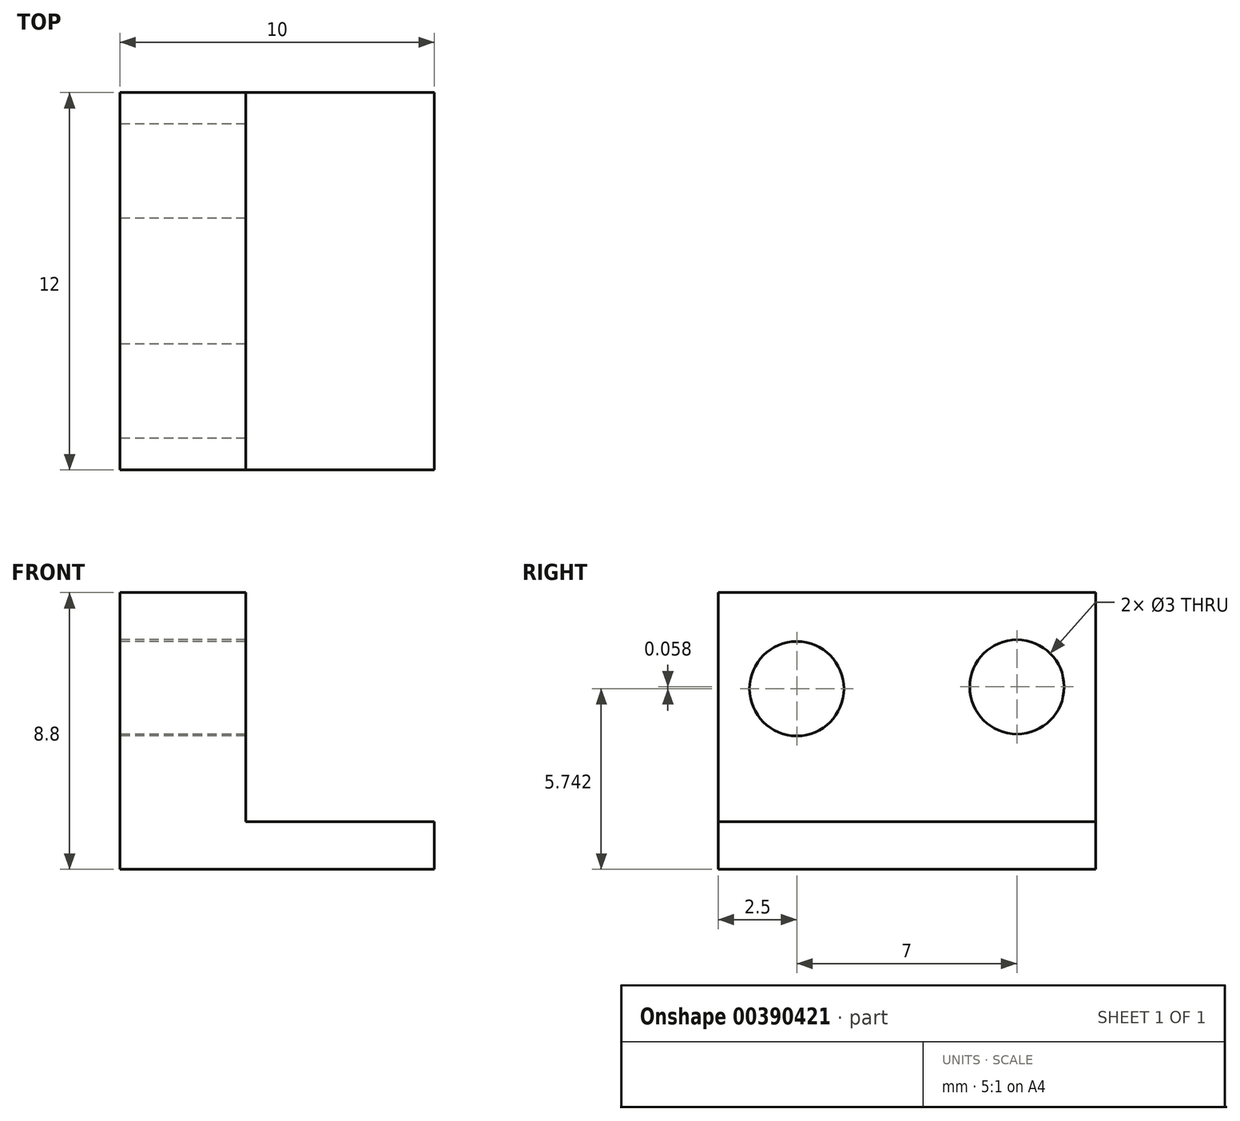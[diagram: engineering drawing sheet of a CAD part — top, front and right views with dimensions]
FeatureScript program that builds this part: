
annotation { "Feature Type Name" : "Feature", "Feature Type Description" : "" }
export const myFeature = defineFeature(function(context is Context, id is Id, definition is map)
    precondition{}
    {
        {
            var Q0;
            Q0=qCreatedBy(makeId("Front.planeOp"),FACE);
            var sketch = newSketch(context, id + "F0", { "sketchPlane" : qUnion([Q0])});
            skLineSegment(sketch, "E0.bottom", {"start": v(2, -4.4) * mm, "end": v(-2, -4.4) * mm});
            skLineSegment(sketch, "E0.top", {"start": v(2, 4.4) * mm, "end": v(-2, 4.4) * mm});
            skLineSegment(sketch, "E0.left", {"start": v(2, -4.4) * mm, "end": v(2, 4.4) * mm});
            skLineSegment(sketch, "E0.right", {"start": v(-2, -4.4) * mm, "end": v(-2, 4.4) * mm});
            skPoint(sketch, "E0.middle", {"position": v(0, 0) * mm});
            skLineSegment(sketch, "E1.bottom", {"start": v(2, -2.89) * mm, "end": v(8, -2.89) * mm});
            skLineSegment(sketch, "E1.top", {"start": v(2, -4.4) * mm, "end": v(8, -4.4) * mm});
            skLineSegment(sketch, "E1.right", {"start": v(8, -2.89) * mm, "end": v(8, -4.4) * mm});
            skSolve(sketch);
        }
        {
            var Q0;
            {var subQ0=sQuery(id+"F0.wireOp",EDGE,"E1.bottom");Q0=makeQuery(id+"F0.imprint","IMPRINT",FACE,{"disambiguationData":[TD([[makeQuery(id+"F0.imprint","IMPRINT",EDGE,{"derivedFrom":subQ0}),-1.0]])]});}
            var Q1;
            {var subQ3=sQuery(id+"F0.wireOp",EDGE,"E0.bottom");Q1=makeQuery(id+"F0.imprint","IMPRINT",FACE,{"disambiguationData":[TD([[makeQuery(id+"F0.imprint","IMPRINT",EDGE,{"derivedFrom":subQ3}),-1.0]])]});}
            extrude(context, id + "F1", {"entities" : qUnion([Q0, Q1]), "depth" : 12 * mm});
        }
        {
            var Q0;
            Q0=makeQuery(id+"F1.opExtrude","SWEPT_FACE",FACE,{"disambiguationData":[OSD([sQuery(id+"F0.wireOp",EDGE,"E0.right")])]});
            var sketch = newSketch(context, id + "F2", { "sketchPlane" : qUnion([Q0])});
            skCircle(sketch, "E2", {"center": v(2.5, 1.4) * mm, "radius": 1.5 * mm});
            skCircle(sketch, "E3", {"center": v(9.5, 1.34) * mm, "radius": 1.5 * mm});
            skSolve(sketch);
        }
        {
            var Q0;
            Q0=makeQuery(id+"F2.imprint","IMPRINT",FACE,{"disambiguationData":[TD([[makeQuery(id+"F2.imprint","IMPRINT",EDGE,{"derivedFrom":sQuery(id+"F2.wireOp",EDGE,"E2")}),1.0]])]});
            var Q1;
            Q1=makeQuery(id+"F2.imprint","IMPRINT",FACE,{"disambiguationData":[TD([[makeQuery(id+"F2.imprint","IMPRINT",EDGE,{"derivedFrom":sQuery(id+"F2.wireOp",EDGE,"E3")}),1.0]])]});
            extrude(context, id + "F3", {"entities" : qUnion([Q0, Q1]), "operationType" : NewBodyOperationType.REMOVE, "oppositeDirection" : true, "depth" : 25 * mm});
        }
    });
